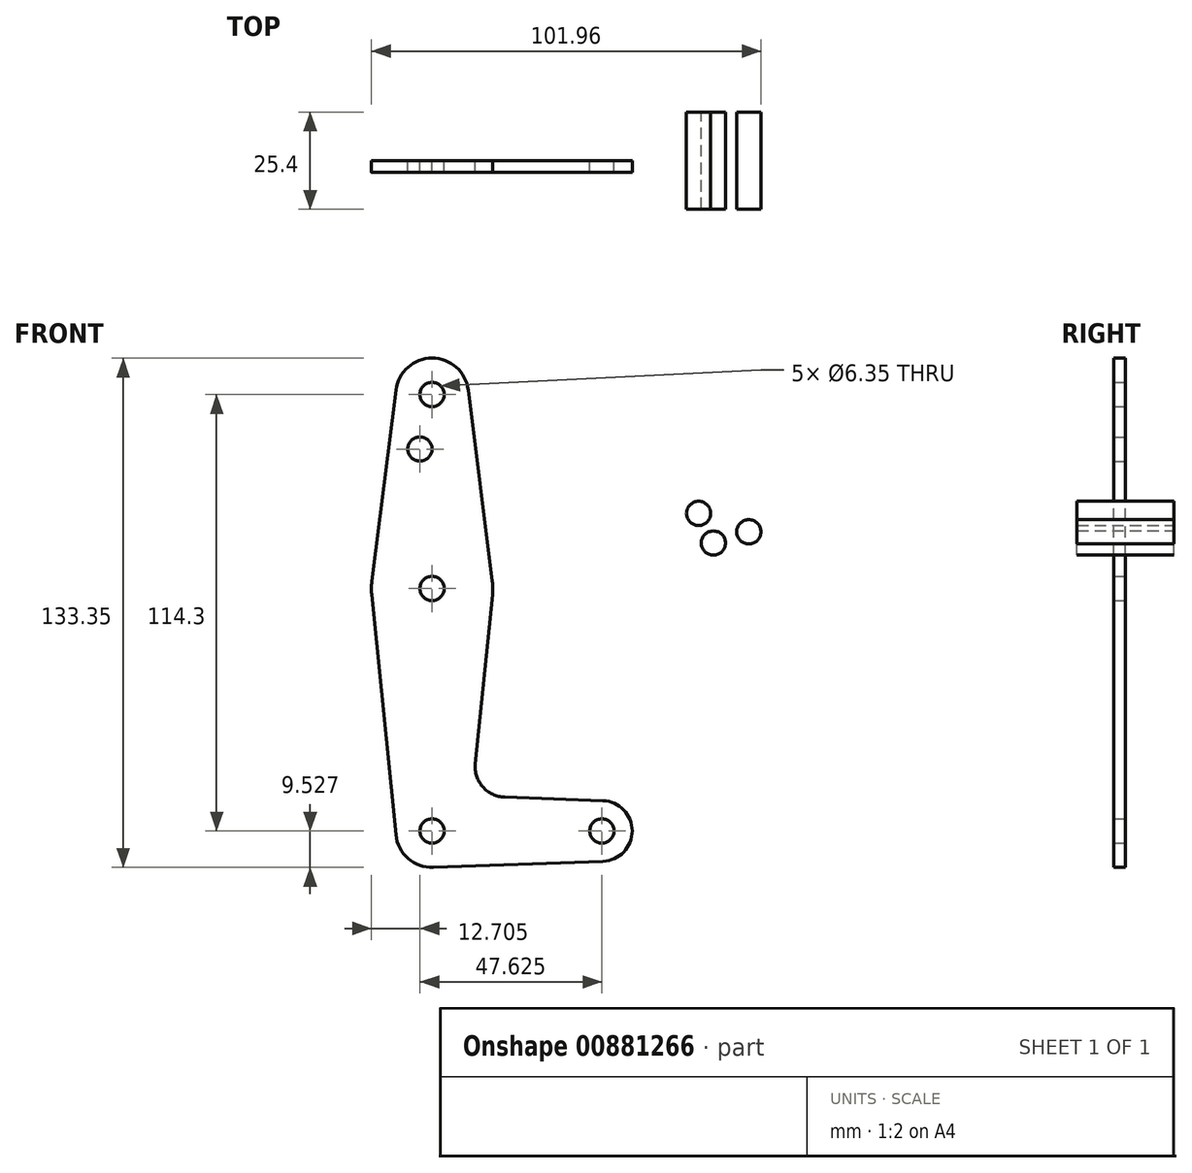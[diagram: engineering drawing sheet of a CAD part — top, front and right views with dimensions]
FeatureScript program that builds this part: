
annotation { "Feature Type Name" : "Feature", "Feature Type Description" : "" }
export const myFeature = defineFeature(function(context is Context, id is Id, definition is map)
    precondition{}
    {
        {
            var Q0;
            Q0=qCreatedBy(makeId("Front.planeOp"),FACE);
            var sketch = newSketch(context, id + "F0", { "sketchPlane" : qUnion([Q0])});
            skLineSegment(sketch, "E0", {"start": v(-50.8, 52.43) * mm, "end": v(-50.8, 1.63) * mm, "construction": true});
            skLineSegment(sketch, "E1", {"start": v(-50.8, 1.63) * mm, "end": v(-50.8, -61.87) * mm, "construction": true});
            skLineSegment(sketch, "E2", {"start": v(-50.8, -61.87) * mm, "end": v(-6.35, -61.87) * mm, "construction": true});
            skCircle(sketch, "E3", {"center": v(-50.8, 52.43) * mm, "radius": 9.53 * mm});
            skCircle(sketch, "E4", {"center": v(-50.8, 1.63) * mm, "radius": 15.88 * mm});
            skCircle(sketch, "E5", {"center": v(-50.8, -61.87) * mm, "radius": 9.53 * mm});
            skCircle(sketch, "E6", {"center": v(-6.35, -61.87) * mm, "radius": 7.94 * mm});
            skLineSegment(sketch, "E7", {"start": v(-60.25, 53.6) * mm, "end": v(-66.8, 1.63) * mm});
            skLineSegment(sketch, "E8", {"start": v(-35.05, 3.61) * mm, "end": v(-41.35, 53.62) * mm});
            skLineSegment(sketch, "E9", {"start": v(-34.85, 1.62) * mm, "end": v(-39.46, -44.28) * mm});
            skLineSegment(sketch, "E10", {"start": v(-66.76, 1.63) * mm, "end": v(-60.28, -62.83) * mm});
            skLineSegment(sketch, "E11", {"start": v(-31.83, -53.02) * mm, "end": v(-6.07, -53.94) * mm});
            skLineSegment(sketch, "E12", {"start": v(-50.8, -71.4) * mm, "end": v(-6.07, -69.8) * mm});
            skCircle(sketch, "E13", {"center": v(-50.8, 52.43) * mm, "radius": 3.18 * mm});
            skCircle(sketch, "E14", {"center": v(-53.98, 38.15) * mm, "radius": 3.18 * mm});
            skCircle(sketch, "E15", {"center": v(-50.8, 1.63) * mm, "radius": 3.18 * mm});
            skCircle(sketch, "E16", {"center": v(-50.8, -61.87) * mm, "radius": 3.18 * mm});
            skCircle(sketch, "E17", {"center": v(-6.35, -61.87) * mm, "radius": 3.18 * mm});
            skArc(sketch, "E18.filletArc", {"start": v(-39.46, -44.28) * mm, "mid": v(-37.54, -50.3) * mm, "end": v(-31.83, -53.02) * mm});
            skSolve(sketch);
        }
        {
            var Q0;
            Q0 = qSketchRegion(id + "F0", true);
            extrude(context, id + "F1", {"entities" : qUnion([Q0]), "depth" : 3.05 * mm, "offsetDistance" : 25.4 * mm});
        }
        {
            var Q0;
            Q0=qCreatedBy(makeId("Front.planeOp"),FACE);
            var sketch = newSketch(context, id + "F2", { "sketchPlane" : qUnion([Q0])});
            skCircle(sketch, "E19", {"center": v(18.97, 21.3) * mm, "radius": 3.18 * mm});
            skSolve(sketch);
        }
        {
            var Q0;
            Q0 = qSketchRegion(id + "F2", true);
            extrude(context, id + "F3", {"entities" : qUnion([Q0]), "endBound" : BoundingType.SYMMETRIC, "depth" : 25.4 * mm, "offsetDistance" : 25.4 * mm});
        }
        {
            var Q0;
            Q0=qCreatedBy(makeId("Front.planeOp"),FACE);
            var sketch = newSketch(context, id + "F4", { "sketchPlane" : qUnion([Q0])});
            skCircle(sketch, "E20.0", {"center": v(22.83, 13.53) * mm, "radius": 3.18 * mm});
            skSolve(sketch);
        }
        {
            var Q0;
            Q0=qCreatedBy(makeId("Front.planeOp"),FACE);
            var sketch = newSketch(context, id + "F5", { "sketchPlane" : qUnion([Q0])});
            skCircle(sketch, "E21", {"center": v(32.1, 16.46) * mm, "radius": 3.18 * mm});
            skSolve(sketch);
        }
        {
            var Q0;
            Q0=makeQuery(id+"F5.imprint","IMPRINT",FACE,{"disambiguationData":[TD([[makeQuery(id+"F5.imprint","IMPRINT",EDGE,{"derivedFrom":sQuery(id+"F5.wireOp",EDGE,"E21")}),1.0]])]});
            var Q1;
            Q1=sQuery(id+"F5.wireOp",EDGE,"E21");
            extrude(context, id + "F6", {"entities" : qUnion([Q0]), "surfaceEntities" : qUnion([Q1]), "endBound" : BoundingType.SYMMETRIC, "depth" : 25.4 * mm, "offsetDistance" : 25.4 * mm});
        }
        {
            var Q0;
            Q0=makeQuery(id+"F4.imprint","IMPRINT",FACE,{"disambiguationData":[TD([[makeQuery(id+"F4.imprint","IMPRINT",EDGE,{"derivedFrom":sQuery(id+"F4.wireOp",EDGE,"E20.0")}),1.0]])]});
            extrude(context, id + "F7", {"entities" : qUnion([Q0]), "endBound" : BoundingType.SYMMETRIC, "depth" : 25.4 * mm, "offsetDistance" : 25.4 * mm});
        }
    });
